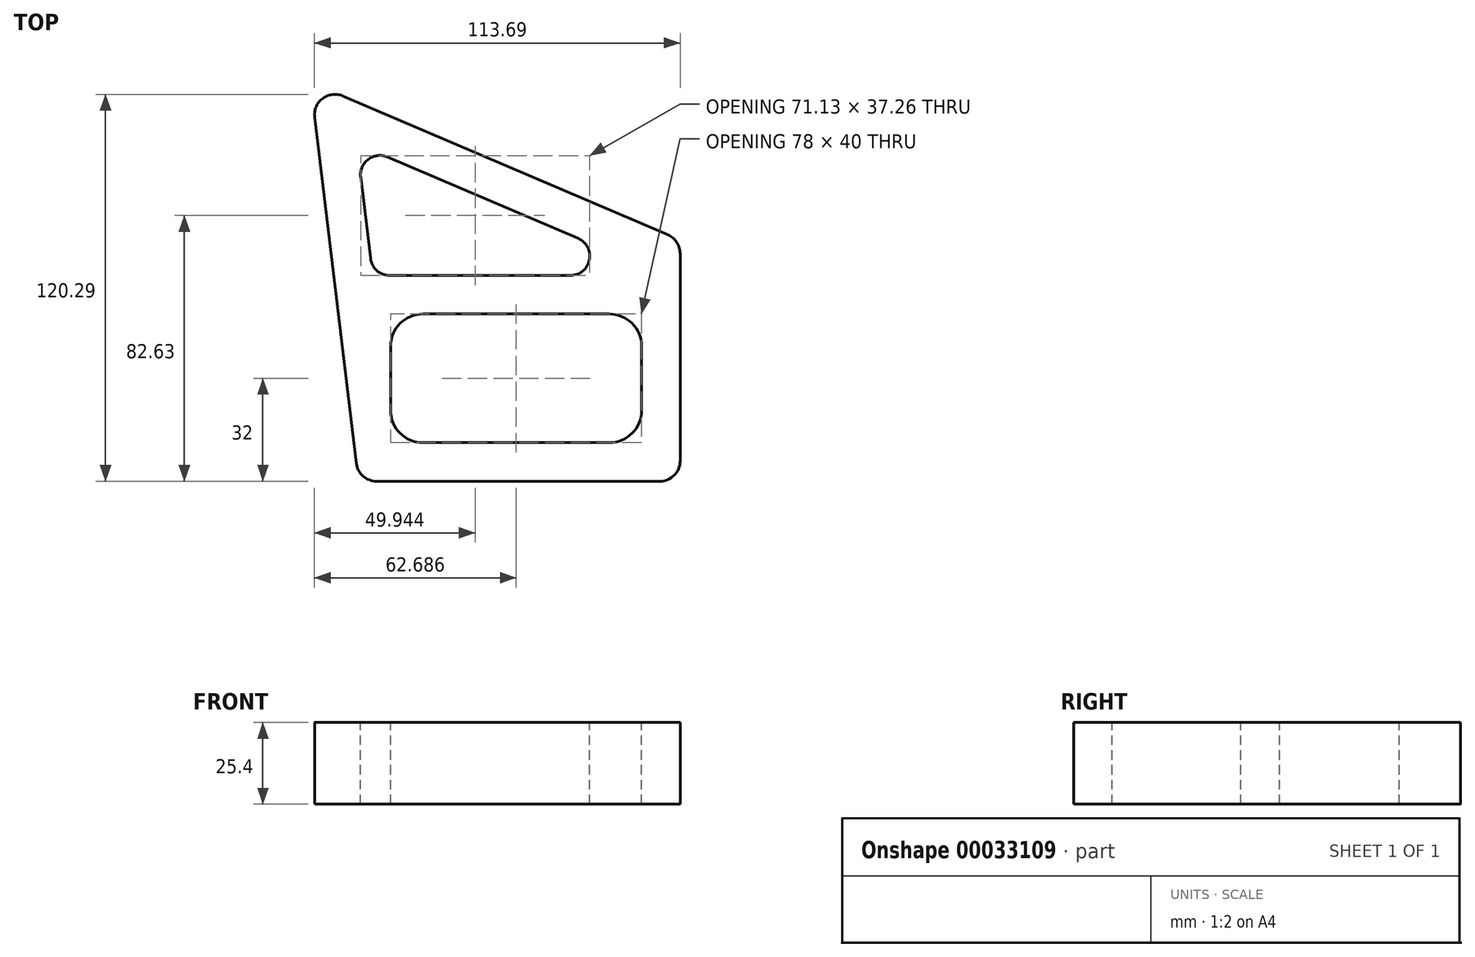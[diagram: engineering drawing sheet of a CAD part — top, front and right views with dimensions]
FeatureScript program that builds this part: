
annotation { "Feature Type Name" : "Feature", "Feature Type Description" : "" }
export const myFeature = defineFeature(function(context is Context, id is Id, definition is map)
    precondition{}
    {
        {
            var Q0;
            Q0=qCreatedBy(makeId("Top.planeOp"),FACE);
            var sketch = newSketch(context, id + "F0", { "sketchPlane" : qUnion([Q0])});
            skLineSegment(sketch, "E0", {"start": v(-57.97, 53.4) * mm, "end": v(-45, -54.2) * mm});
            skLineSegment(sketch, "E1", {"start": v(-38.7, -59.8) * mm, "end": v(49.32, -59.8) * mm});
            skLineSegment(sketch, "E2", {"start": v(55.67, -53.44) * mm, "end": v(55.67, 11.02) * mm});
            skLineSegment(sketch, "E3", {"start": v(51.81, 16.86) * mm, "end": v(-49.17, 60) * mm});
            skPoint(sketch, "E4.visualSharp", {"position": v(-44.33, -59.8) * mm});
            skArc(sketch, "E4.filletArc", {"start": v(-45, -54.2) * mm, "mid": v(-42.92, -58.2) * mm, "end": v(-38.7, -59.8) * mm});
            skPoint(sketch, "E5.visualSharp", {"position": v(55.67, -59.8) * mm});
            skArc(sketch, "E5.filletArc", {"start": v(49.32, -59.8) * mm, "mid": v(53.8, -57.93) * mm, "end": v(55.67, -53.44) * mm});
            skPoint(sketch, "E6.visualSharp", {"position": v(55.67, 15.2) * mm});
            skArc(sketch, "E6.filletArc", {"start": v(55.67, 11.02) * mm, "mid": v(54.62, 14.52) * mm, "end": v(51.81, 16.86) * mm});
            skPoint(sketch, "E7.visualSharp", {"position": v(-59.29, 64.31) * mm});
            skArc(sketch, "E7.filletArc", {"start": v(-49.17, 60) * mm, "mid": v(-55.48, 59.23) * mm, "end": v(-57.97, 53.4) * mm});
            skSolve(sketch);
        }
        {
            var Q0;
            Q0 = qSketchRegion(id + "F0", true);
            extrude(context, id + "F1", {"entities" : qUnion([Q0]), "depth" : 25.4 * mm});
        }
        {
            var Q0;
            Q0=makeQuery(id+"F1.opExtrude","CAP_FACE",FACE,{"disambiguationData":[OSD([sQuery(id+"F0.wireOp",EDGE,"E0"),sQuery(id+"F0.wireOp",EDGE,"E1"),sQuery(id+"F0.wireOp",EDGE,"E2"),sQuery(id+"F0.wireOp",EDGE,"E3"),sQuery(id+"F0.wireOp",EDGE,"E4.filletArc"),sQuery(id+"F0.wireOp",EDGE,"E5.filletArc"),sQuery(id+"F0.wireOp",EDGE,"E6.filletArc"),sQuery(id+"F0.wireOp",EDGE,"E7.filletArc")])],"isStart":false});
            var sketch = newSketch(context, id + "F2", { "sketchPlane" : qUnion([Q0])});
            skLineSegment(sketch, "E8.bottom", {"start": v(-24.33, -7.8) * mm, "end": v(33.67, -7.8) * mm});
            skLineSegment(sketch, "E8.top", {"start": v(-24.33, -47.8) * mm, "end": v(33.67, -47.8) * mm});
            skLineSegment(sketch, "E8.left", {"start": v(-34.33, -17.8) * mm, "end": v(-34.33, -37.8) * mm});
            skLineSegment(sketch, "E8.right", {"start": v(43.67, -17.8) * mm, "end": v(43.67, -37.8) * mm});
            skPoint(sketch, "E9.visualSharp", {"position": v(-34.33, -47.8) * mm});
            skArc(sketch, "E9.filletArc", {"start": v(-34.33, -37.8) * mm, "mid": v(-31.4, -44.86) * mm, "end": v(-24.33, -47.8) * mm});
            skPoint(sketch, "E10.visualSharp", {"position": v(-34.33, -7.8) * mm});
            skArc(sketch, "E10.filletArc", {"start": v(-24.33, -7.8) * mm, "mid": v(-31.4, -10.72) * mm, "end": v(-34.33, -17.8) * mm});
            skPoint(sketch, "E11.visualSharp", {"position": v(43.67, -7.8) * mm});
            skArc(sketch, "E11.filletArc", {"start": v(43.67, -17.8) * mm, "mid": v(40.74, -10.72) * mm, "end": v(33.67, -7.8) * mm});
            skPoint(sketch, "E12.visualSharp", {"position": v(43.67, -47.8) * mm});
            skArc(sketch, "E12.filletArc", {"start": v(33.67, -47.8) * mm, "mid": v(40.74, -44.86) * mm, "end": v(43.67, -37.8) * mm});
            skSolve(sketch);
        }
        {
            var Q0;
            Q0=makeQuery(id+"F2.imprint","IMPRINT",FACE,{"disambiguationData":[TD([[makeQuery(id+"F2.imprint","IMPRINT",EDGE,{"derivedFrom":sQuery(id+"F2.wireOp",EDGE,"E8.bottom")}),-1.0]])]});
            extrude(context, id + "F3", {"entities" : qUnion([Q0]), "operationType" : NewBodyOperationType.REMOVE, "endBound" : BoundingType.UP_TO_NEXT, "oppositeDirection" : true, "depth" : 25.4 * mm});
        }
        {
            var Q0;
            Q0=makeQuery(id+"F1.opExtrude","CAP_FACE",FACE,{"disambiguationData":[OSD([sQuery(id+"F0.wireOp",EDGE,"E0"),sQuery(id+"F0.wireOp",EDGE,"E1"),sQuery(id+"F0.wireOp",EDGE,"E2"),sQuery(id+"F0.wireOp",EDGE,"E3"),sQuery(id+"F0.wireOp",EDGE,"E4.filletArc"),sQuery(id+"F0.wireOp",EDGE,"E5.filletArc"),sQuery(id+"F0.wireOp",EDGE,"E6.filletArc"),sQuery(id+"F0.wireOp",EDGE,"E7.filletArc")])],"isStart":false});
            var sketch = newSketch(context, id + "F4", { "sketchPlane" : qUnion([Q0])});
            skLineSegment(sketch, "E13", {"start": v(21.55, 4.2) * mm, "end": v(-34.64, 4.2) * mm});
            skLineSegment(sketch, "E14", {"start": v(-40.6, 9.5) * mm, "end": v(-43.64, 34.8) * mm});
            skLineSegment(sketch, "E15", {"start": v(-35.33, 41.03) * mm, "end": v(23.9, 15.73) * mm});
            skPoint(sketch, "E16.visualSharp", {"position": v(-44.89, 45.11) * mm});
            skArc(sketch, "E16.filletArc", {"start": v(-35.33, 41.03) * mm, "mid": v(-41.29, 40.31) * mm, "end": v(-43.64, 34.8) * mm});
            skPoint(sketch, "E17.visualSharp", {"position": v(-39.96, 4.2) * mm});
            skArc(sketch, "E17.filletArc", {"start": v(-40.6, 9.5) * mm, "mid": v(-38.62, 5.72) * mm, "end": v(-34.64, 4.2) * mm});
            skPoint(sketch, "E18.visualSharp", {"position": v(50.87, 4.2) * mm});
            skArc(sketch, "E18.filletArc", {"start": v(21.55, 4.2) * mm, "mid": v(27.43, 9) * mm, "end": v(23.9, 15.73) * mm});
            skSolve(sketch);
        }
        {
            var Q0;
            Q0=makeQuery(id+"F4.imprint","IMPRINT",FACE,{"disambiguationData":[TD([[makeQuery(id+"F4.imprint","IMPRINT",EDGE,{"derivedFrom":sQuery(id+"F4.wireOp",EDGE,"E13")}),-1.0]])]});
            extrude(context, id + "F5", {"entities" : qUnion([Q0]), "operationType" : NewBodyOperationType.REMOVE, "endBound" : BoundingType.UP_TO_NEXT, "oppositeDirection" : true, "depth" : 25 * mm});
        }
    });
